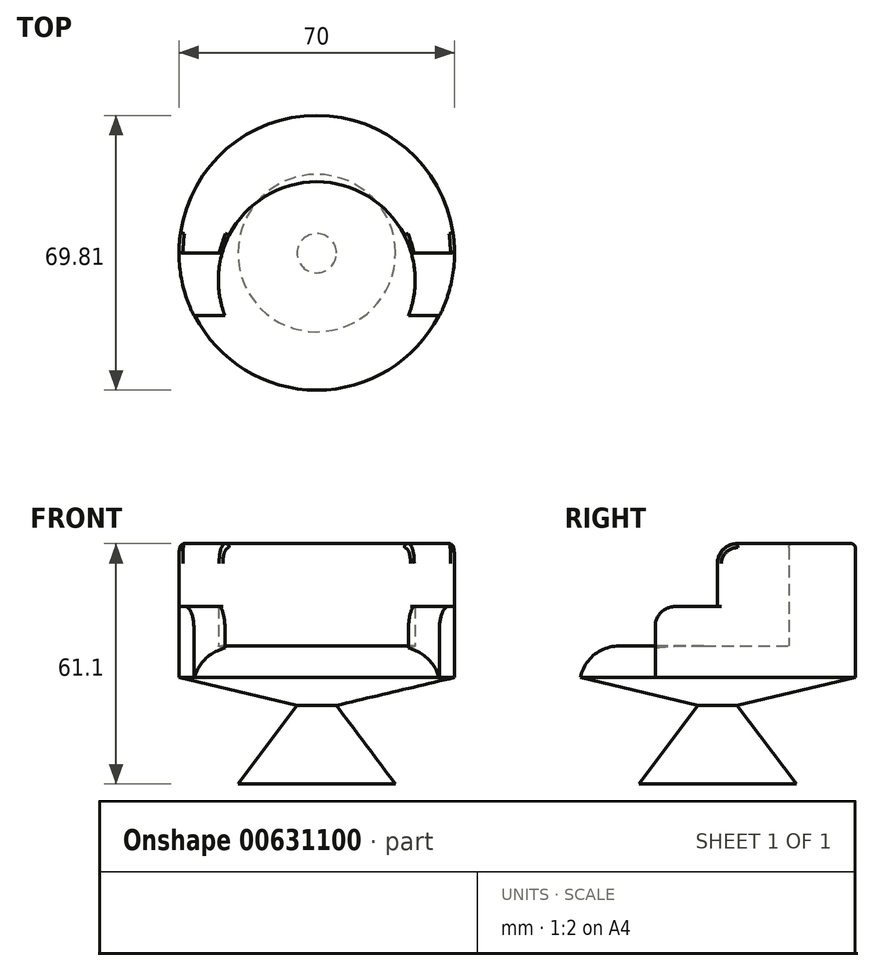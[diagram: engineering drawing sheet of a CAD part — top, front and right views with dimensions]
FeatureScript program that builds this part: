
annotation { "Feature Type Name" : "Feature", "Feature Type Description" : "" }
export const myFeature = defineFeature(function(context is Context, id is Id, definition is map)
    precondition{}
    {
        {
            var Q0;
            Q0=qCreatedBy(makeId("Top.planeOp"),FACE);
            cPlane(context, id + "F0", {"entities" : qUnion([Q0]), "cplaneType" : CPlaneType.OFFSET, "offset" : 35 * mm, "oppositeDirection" : true, "width" : 150 * mm, "height" : 150 * mm});
        }
        {
            var Q0;
            Q0=qCreatedBy(id+"F0.planeOp",FACE);
            cPlane(context, id + "F1", {"entities" : qUnion([Q0]), "cplaneType" : CPlaneType.OFFSET, "offset" : 20 * mm, "width" : 150 * mm, "height" : 150 * mm});
        }
        {
            var Q0;
            Q0=qCreatedBy(id+"F0.planeOp",FACE);
            var sketch = newSketch(context, id + "F2", { "sketchPlane" : qUnion([Q0])});
            skCircle(sketch, "E0", {"center": v(0, 0) * mm, "radius": 20 * mm});
            skSolve(sketch);
        }
        {
            var Q0;
            Q0=qCreatedBy(id+"F1.planeOp",FACE);
            var sketch = newSketch(context, id + "F3", { "sketchPlane" : qUnion([Q0])});
            skCircle(sketch, "E1", {"center": v(0, 0) * mm, "radius": 5 * mm});
            skSolve(sketch);
        }
        {
            var Q0;
            Q0=makeQuery(id+"F2.imprint","IMPRINT",FACE,{"disambiguationData":[TD([[makeQuery(id+"F2.imprint","IMPRINT",EDGE,{"derivedFrom":sQuery(id+"F2.wireOp",EDGE,"E0")}),1.0]])]});
            var Q1;
            Q1=makeQuery(id+"F3.imprint","IMPRINT",FACE,{"disambiguationData":[TD([[makeQuery(id+"F3.imprint","IMPRINT",EDGE,{"derivedFrom":sQuery(id+"F3.wireOp",EDGE,"E1")}),1.0]])]});
            loft(context, id + "F4", {"sheetProfilesArray" : [{ "sheetProfileEntities" : qUnion([Q0]) }, { "sheetProfileEntities" : qUnion([Q1]) }]});
        }
        {
            var Q0;
            Q0=qCreatedBy(makeId("Top.planeOp"),FACE);
            cPlane(context, id + "F5", {"entities" : qUnion([Q0]), "cplaneType" : CPlaneType.OFFSET, "offset" : 7.9 * mm, "oppositeDirection" : true, "width" : 150 * mm, "height" : 150 * mm});
        }
        {
            var Q0;
            Q0=qCreatedBy(id+"F5.planeOp",FACE);
            var sketch = newSketch(context, id + "F6", { "sketchPlane" : qUnion([Q0])});
            skCircle(sketch, "E2", {"center": v(0, 0) * mm, "radius": 35 * mm});
            skSolve(sketch);
        }
        {
            var Q1;
            Q1 = qSketchRegion(id + "F6", true);
            var Q2;
            Q2 = qSketchRegion(id + "F3", true);
            loft(context, id + "F7", {"operationType" : NewBodyOperationType.ADD, "sheetProfilesArray" : [{ "sheetProfileEntities" : qUnion([Q1]) }, { "sheetProfileEntities" : qUnion([Q2]) }]});
        }
        {
            var Q0;
            Q0=makeQuery(id+"F7.opLoft","CAP_FACE",FACE,{"disambiguationData":[OSD([makeQuery(id+"F6.imprint","IMPRINT",FACE,{"disambiguationData":[TD([[makeQuery(id+"F6.imprint","IMPRINT",EDGE,{"derivedFrom":sQuery(id+"F6.wireOp",EDGE,"E2")}),1.0]])]})])],"isStart":true});
            extrude(context, id + "F8", {"entities" : qUnion([Q0]), "operationType" : NewBodyOperationType.ADD, "depth" : 8 * mm, "offsetDistance" : 25 * mm});
        }
        {
            var Q0;
            Q0=makeQuery(id+"F8.opExtrude","CAP_FACE",FACE,{"disambiguationData":[OSD([makeQuery(id+"F6.imprint","IMPRINT",FACE,{"disambiguationData":[TD([[makeQuery(id+"F6.imprint","IMPRINT",EDGE,{"derivedFrom":sQuery(id+"F6.wireOp",EDGE,"E2")}),1.0]])]})])],"isStart":false});
            var sketch = newSketch(context, id + "F9", { "sketchPlane" : qUnion([Q0])});
            skCircle(sketch, "E3", {"center": v(0, -6.88) * mm, "radius": 25 * mm});
            skLineSegment(sketch, "E4", {"start": v(-35, 0) * mm, "end": v(-24.04, 0) * mm});
            skLineSegment(sketch, "E5", {"start": v(24.04, 0) * mm, "end": v(35, 0) * mm});
            skLineSegment(sketch, "E6", {"start": v(-29.11, -19.43) * mm, "end": v(-23.22, -16.14) * mm});
            skLineSegment(sketch, "E7", {"start": v(23.22, -16.14) * mm, "end": v(29.08, -19.48) * mm});
            skSolve(sketch);
        }
        {
            var Q0;
            {var subQ0=sQuery(id+"F9.wireOp",EDGE,"E4");Q0=makeQuery(id+"F9.imprint","IMPRINT",FACE,{"disambiguationData":[TD([[makeQuery(id+"F9.imprint","IMPRINT",EDGE,{"derivedFrom":subQ0}),1.0]])]});}
            extrude(context, id + "F10", {"entities" : qUnion([Q0]), "operationType" : NewBodyOperationType.ADD, "depth" : 26 * mm, "offsetDistance" : 25 * mm});
        }
        {
            var Q0;
            Q0=makeQuery(id+"F8.opExtrude","CAP_FACE",FACE,{"disambiguationData":[OSD([makeQuery(id+"F6.imprint","IMPRINT",FACE,{"disambiguationData":[TD([[makeQuery(id+"F6.imprint","IMPRINT",EDGE,{"derivedFrom":sQuery(id+"F6.wireOp",EDGE,"E2")}),1.0]])]})])],"isStart":false});
            var sketch = newSketch(context, id + "F11", { "sketchPlane" : qUnion([Q0])});
            skCircle(sketch, "E8", {"center": v(0, -6.88) * mm, "radius": 25 * mm});
            skLineSegment(sketch, "E9", {"start": v(-31.22, -15.82) * mm, "end": v(-23.35, -15.82) * mm});
            skLineSegment(sketch, "E10", {"start": v(23.35, -15.82) * mm, "end": v(31.22, -15.82) * mm});
            skSolve(sketch);
        }
        {
            var Q0;
            {var subQ2=sQuery(id+"F11.wireOp",EDGE,"E9");Q0=makeQuery(id+"F11.imprint","IMPRINT",FACE,{"disambiguationData":[TD([[makeQuery(id+"F11.imprint","IMPRINT",EDGE,{"derivedFrom":subQ2}),1.0]])]});}
            var Q1;
            {var subQ2=sQuery(id+"F11.wireOp",EDGE,"E10");Q1=makeQuery(id+"F11.imprint","IMPRINT",FACE,{"disambiguationData":[TD([[makeQuery(id+"F11.imprint","IMPRINT",EDGE,{"derivedFrom":subQ2}),1.0]])]});}
            extrude(context, id + "F12", {"entities" : qUnion([Q0, Q1]), "operationType" : NewBodyOperationType.ADD, "depth" : 10 * mm, "offsetDistance" : 25 * mm});
        }
        {
            var Q0;
            Q0=makeQuery(id+"F10.opExtrude","CAP_EDGE",EDGE,{"disambiguationData":[OSD([sQuery(id+"F9.wireOp",EDGE,"E4")])],"isStart":false});
            var Q1;
            Q1=makeQuery(id+"F10.opExtrude","CAP_EDGE",EDGE,{"disambiguationData":[OSD([sQuery(id+"F9.wireOp",EDGE,"E5")])],"isStart":false});
            var Q2;
            Q2=makeQuery(id+"F12.opExtrude","CAP_EDGE",EDGE,{"disambiguationData":[OSD([sQuery(id+"F11.wireOp",EDGE,"E9")])],"isStart":false});
            var Q3;
            Q3=makeQuery(id+"F12.opExtrude","CAP_EDGE",EDGE,{"disambiguationData":[OSD([sQuery(id+"F11.wireOp",EDGE,"E10")])],"isStart":false});
            fillet(context, id + "F13", {"entities" : qUnion([Q0, Q1, Q2, Q3]), "radius" : 5 * mm, "tangentPropagation" : true, "allowEdgeOverflow" : false});
        }
        {
            var Q0;
            Q0=makeQuery(id+"F8.opExtrude","CAP_EDGE",EDGE,{"disambiguationData":[OSD([sQuery(id+"F6.wireOp",EDGE,"E2")])],"isStart":false});
            fillet(context, id + "F14", {"entities" : qUnion([Q0]), "radius" : 10 * mm, "tangentPropagation" : true, "allowEdgeOverflow" : false});
        }
        {
            var Q0;
            Q0=makeQuery(id+"F10.opExtrude","CAP_EDGE",EDGE,{"disambiguationData":[OSD([sQuery(id+"F9.wireOp",EDGE,"E3")])],"isStart":false});
            fillet(context, id + "F15", {"entities" : qUnion([Q0]), "radius" : 1 * mm, "tangentPropagation" : true, "allowEdgeOverflow" : false});
        }
        {
            var Q0;
            Q0=makeQuery(id+"F10.opExtrude","CAP_EDGE",EDGE,{"disambiguationData":[OSD([sQuery(id+"F6.wireOp",EDGE,"E2")])],"isStart":false});
            fillet(context, id + "F16", {"entities" : qUnion([Q0]), "radius" : 1 * mm, "tangentPropagation" : true, "allowEdgeOverflow" : false});
        }
    });
